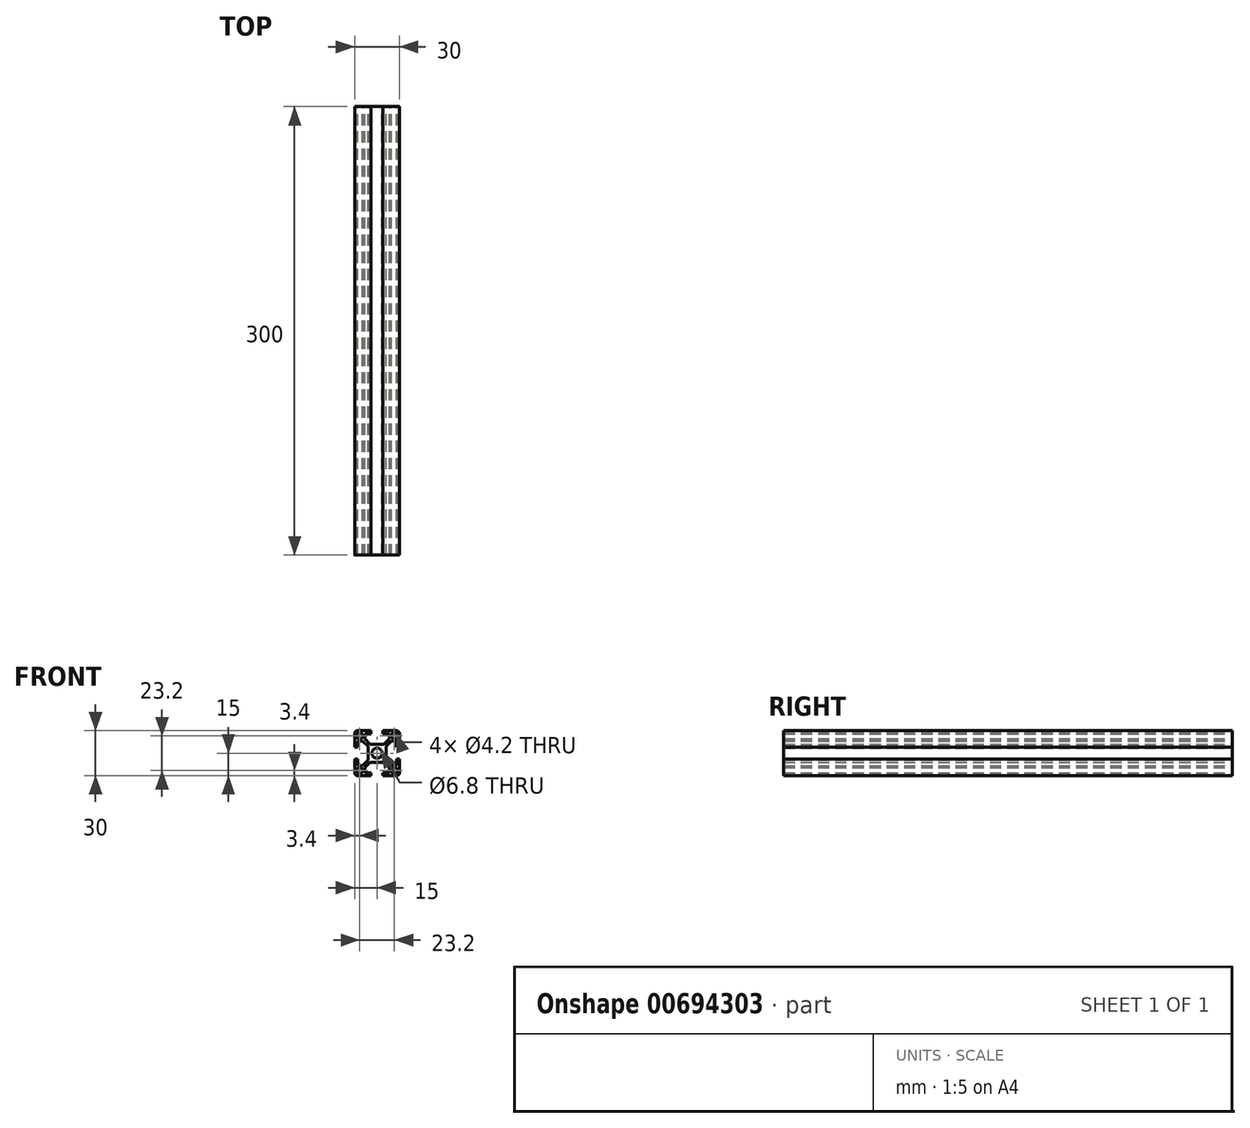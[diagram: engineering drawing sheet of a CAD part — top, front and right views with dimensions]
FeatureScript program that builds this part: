
annotation { "Feature Type Name" : "Feature", "Feature Type Description" : "" }
export const myFeature = defineFeature(function(context is Context, id is Id, definition is map)
    precondition{}
    {
        {
            var Q0;
            Q0=qCreatedBy(makeId("Front.planeOp"),FACE);
            var sketch = newSketch(context, id + "F0", { "sketchPlane" : qUnion([Q0])});
            skLineSegment(sketch, "E0", {"start": v(0, 6) * mm, "end": v(-4.59, 6) * mm});
            skLineSegment(sketch, "E1", {"start": v(-4.59, 6) * mm, "end": v(-8.25, 9.66) * mm});
            skLineSegment(sketch, "E2", {"start": v(-8.25, 9.66) * mm, "end": v(-8.25, 13) * mm});
            skLineSegment(sketch, "E3", {"start": v(-8.25, 13) * mm, "end": v(-4, 13) * mm});
            skLineSegment(sketch, "E4", {"start": v(-4, 13) * mm, "end": v(-4, 15) * mm});
            skLineSegment(sketch, "E5", {"start": v(-4, 15) * mm, "end": v(-13, 15) * mm});
            skLineSegment(sketch, "E6", {"start": v(-15, 13) * mm, "end": v(-15, 4) * mm});
            skLineSegment(sketch, "E7", {"start": v(-15, 4) * mm, "end": v(-13, 4) * mm});
            skLineSegment(sketch, "E8", {"start": v(-13, 4) * mm, "end": v(-13, 8.25) * mm});
            skLineSegment(sketch, "E9", {"start": v(-13, 8.25) * mm, "end": v(-9.66, 8.25) * mm});
            skLineSegment(sketch, "E10", {"start": v(-9.66, 8.25) * mm, "end": v(-6, 4.59) * mm});
            skLineSegment(sketch, "E11", {"start": v(-6, 4.59) * mm, "end": v(-6, 0) * mm});
            skLineSegment(sketch, "E12", {"start": v(-6, 0) * mm, "end": v(0, 0) * mm, "construction": true});
            skLineSegment(sketch, "E13", {"start": v(0, 0) * mm, "end": v(0, 6) * mm, "construction": true});
            skArc(sketch, "E14", {"start": v(0, 3.4) * mm, "mid": v(-2.4, 2.4) * mm, "end": v(-3.4, 0) * mm});
            skCircle(sketch, "E15", {"center": v(-11.6, 11.6) * mm, "radius": 2.1 * mm});
            skLineSegment(sketch, "E16", {"start": v(0, 0) * mm, "end": v(-7.38, 7.38) * mm, "construction": true});
            skLineSegment(sketch, "E17.1.0", {"start": v(-8.25, -13) * mm, "end": v(-8.25, -9.66) * mm});
            skLineSegment(sketch, "E17.1.1", {"start": v(-4, -15) * mm, "end": v(-4, -13) * mm});
            skLineSegment(sketch, "E17.1.2", {"start": v(-4, -13) * mm, "end": v(-8.25, -13) * mm});
            skLineSegment(sketch, "E17.1.3", {"start": v(-15, -4) * mm, "end": v(-15, -13) * mm});
            skLineSegment(sketch, "E17.1.4", {"start": v(-8.25, -9.66) * mm, "end": v(-4.59, -6) * mm});
            skLineSegment(sketch, "E17.1.5", {"start": v(-13, -15) * mm, "end": v(-4, -15) * mm});
            skLineSegment(sketch, "E17.1.6", {"start": v(-4.59, -6) * mm, "end": v(0, -6) * mm});
            skLineSegment(sketch, "E17.1.7", {"start": v(0, -6) * mm, "end": v(0, 0) * mm, "construction": true});
            skLineSegment(sketch, "E17.1.8", {"start": v(0, 0) * mm, "end": v(-6, 0) * mm, "construction": true});
            skLineSegment(sketch, "E17.1.9", {"start": v(-13, -4) * mm, "end": v(-15, -4) * mm});
            skLineSegment(sketch, "E17.1.10", {"start": v(-13, -8.25) * mm, "end": v(-13, -4) * mm});
            skArc(sketch, "E17.1.11", {"start": v(-3.4, 0) * mm, "mid": v(-2.4, -2.4) * mm, "end": v(0, -3.4) * mm});
            skLineSegment(sketch, "E17.1.12", {"start": v(-9.66, -8.25) * mm, "end": v(-13, -8.25) * mm});
            skLineSegment(sketch, "E17.1.13", {"start": v(0, 0) * mm, "end": v(-7.38, -7.38) * mm, "construction": true});
            skLineSegment(sketch, "E17.1.14", {"start": v(-6, -4.59) * mm, "end": v(-9.66, -8.25) * mm});
            skCircle(sketch, "E17.1.15", {"center": v(-11.6, -11.6) * mm, "radius": 2.1 * mm});
            skLineSegment(sketch, "E17.1.16", {"start": v(-6, 0) * mm, "end": v(-6, -4.59) * mm});
            skLineSegment(sketch, "E17.2.0", {"start": v(13, -8.25) * mm, "end": v(9.66, -8.25) * mm});
            skLineSegment(sketch, "E17.2.1", {"start": v(15, -4) * mm, "end": v(13, -4) * mm});
            skLineSegment(sketch, "E17.2.2", {"start": v(13, -4) * mm, "end": v(13, -8.25) * mm});
            skLineSegment(sketch, "E17.2.3", {"start": v(4, -15) * mm, "end": v(13, -15) * mm});
            skLineSegment(sketch, "E17.2.4", {"start": v(9.66, -8.25) * mm, "end": v(6, -4.59) * mm});
            skLineSegment(sketch, "E17.2.5", {"start": v(15, -13) * mm, "end": v(15, -4) * mm});
            skLineSegment(sketch, "E17.2.6", {"start": v(6, -4.59) * mm, "end": v(6, 0) * mm});
            skLineSegment(sketch, "E17.2.7", {"start": v(6, 0) * mm, "end": v(0, 0) * mm, "construction": true});
            skLineSegment(sketch, "E17.2.8", {"start": v(0, 0) * mm, "end": v(0, -6) * mm, "construction": true});
            skLineSegment(sketch, "E17.2.9", {"start": v(4, -13) * mm, "end": v(4, -15) * mm});
            skLineSegment(sketch, "E17.2.10", {"start": v(8.25, -13) * mm, "end": v(4, -13) * mm});
            skArc(sketch, "E17.2.11", {"start": v(0, -3.4) * mm, "mid": v(2.4, -2.4) * mm, "end": v(3.4, 0) * mm});
            skLineSegment(sketch, "E17.2.12", {"start": v(8.25, -9.66) * mm, "end": v(8.25, -13) * mm});
            skLineSegment(sketch, "E17.2.13", {"start": v(0, 0) * mm, "end": v(7.38, -7.38) * mm, "construction": true});
            skLineSegment(sketch, "E17.2.14", {"start": v(4.59, -6) * mm, "end": v(8.25, -9.66) * mm});
            skCircle(sketch, "E17.2.15", {"center": v(11.6, -11.6) * mm, "radius": 2.1 * mm});
            skLineSegment(sketch, "E17.2.16", {"start": v(0, -6) * mm, "end": v(4.59, -6) * mm});
            skLineSegment(sketch, "E17.3.0", {"start": v(8.25, 13) * mm, "end": v(8.25, 9.66) * mm});
            skLineSegment(sketch, "E17.3.1", {"start": v(4, 15) * mm, "end": v(4, 13) * mm});
            skLineSegment(sketch, "E17.3.2", {"start": v(4, 13) * mm, "end": v(8.25, 13) * mm});
            skLineSegment(sketch, "E17.3.3", {"start": v(15, 4) * mm, "end": v(15, 13) * mm});
            skLineSegment(sketch, "E17.3.4", {"start": v(8.25, 9.66) * mm, "end": v(4.59, 6) * mm});
            skLineSegment(sketch, "E17.3.5", {"start": v(13, 15) * mm, "end": v(4, 15) * mm});
            skLineSegment(sketch, "E17.3.6", {"start": v(4.59, 6) * mm, "end": v(0, 6) * mm});
            skLineSegment(sketch, "E17.3.7", {"start": v(0, 6) * mm, "end": v(0, 0) * mm, "construction": true});
            skLineSegment(sketch, "E17.3.8", {"start": v(0, 0) * mm, "end": v(6, 0) * mm, "construction": true});
            skLineSegment(sketch, "E17.3.9", {"start": v(13, 4) * mm, "end": v(15, 4) * mm});
            skLineSegment(sketch, "E17.3.10", {"start": v(13, 8.25) * mm, "end": v(13, 4) * mm});
            skArc(sketch, "E17.3.11", {"start": v(3.4, 0) * mm, "mid": v(2.4, 2.4) * mm, "end": v(0, 3.4) * mm});
            skLineSegment(sketch, "E17.3.12", {"start": v(9.66, 8.25) * mm, "end": v(13, 8.25) * mm});
            skLineSegment(sketch, "E17.3.13", {"start": v(0, 0) * mm, "end": v(7.38, 7.38) * mm, "construction": true});
            skLineSegment(sketch, "E17.3.14", {"start": v(6, 4.59) * mm, "end": v(9.66, 8.25) * mm});
            skCircle(sketch, "E17.3.15", {"center": v(11.6, 11.6) * mm, "radius": 2.1 * mm});
            skLineSegment(sketch, "E17.3.16", {"start": v(6, 0) * mm, "end": v(6, 4.59) * mm});
            skPoint(sketch, "E18.visualSharp", {"position": v(-15, 15) * mm});
            skArc(sketch, "E18.filletArc", {"start": v(-13, 15) * mm, "mid": v(-14.41, 14.41) * mm, "end": v(-15, 13) * mm});
            skPoint(sketch, "E19.visualSharp", {"position": v(15, 15) * mm});
            skArc(sketch, "E19.filletArc", {"start": v(15, 13) * mm, "mid": v(14.41, 14.41) * mm, "end": v(13, 15) * mm});
            skPoint(sketch, "E20.visualSharp", {"position": v(15, -15) * mm});
            skArc(sketch, "E20.filletArc", {"start": v(13, -15) * mm, "mid": v(14.41, -14.41) * mm, "end": v(15, -13) * mm});
            skPoint(sketch, "E21.visualSharp", {"position": v(-15, -15) * mm});
            skArc(sketch, "E21.filletArc", {"start": v(-15, -13) * mm, "mid": v(-14.41, -14.41) * mm, "end": v(-13, -15) * mm});
            skSolve(sketch);
        }
        {
            var Q0;
            Q0=qSketchRegion(id+"F0",true);
            extrude(context, id + "F1", {"entities" : qUnion([Q0]), "depth" : 300 * mm, "offsetDistance" : 25 * mm});
        }
    });
